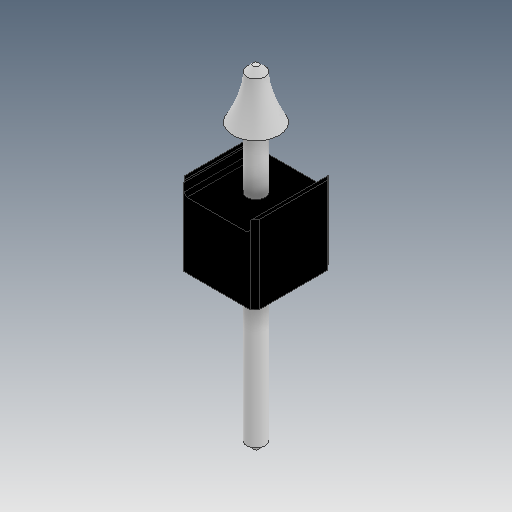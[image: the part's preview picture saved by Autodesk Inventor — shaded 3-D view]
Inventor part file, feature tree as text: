
AUTODESK INVENTOR PART (.ipt)
format: ipt  version: 2020 (Build 240168000, 168)  size: 145,920 bytes
history: native  units: in
note: dims shown in document units (in); Inventor stores cm internally (conversion verified against a paired STEP export)
features: other x4, sketch x4, plane x1
ambient origin geometry x8: Origin, YZ Plane, XZ Plane, XY Plane, X Axis, Y Axis, Z Axis, Center Point
bodies: Solid1 (feature_tree)
feature tree (9):
  other  "pins.ipt"
  other  "Solid2::pins.ipt"
  other  "TaggingFeature1"
  sketch  "Sketch5"  dims[d0=0.3937in]
  sketch  "Sketch6"
  sketch  "Sketch7"
  sketch  "Sketch8"
  plane  "Work Plane1"
  other  "Work Axis1"
